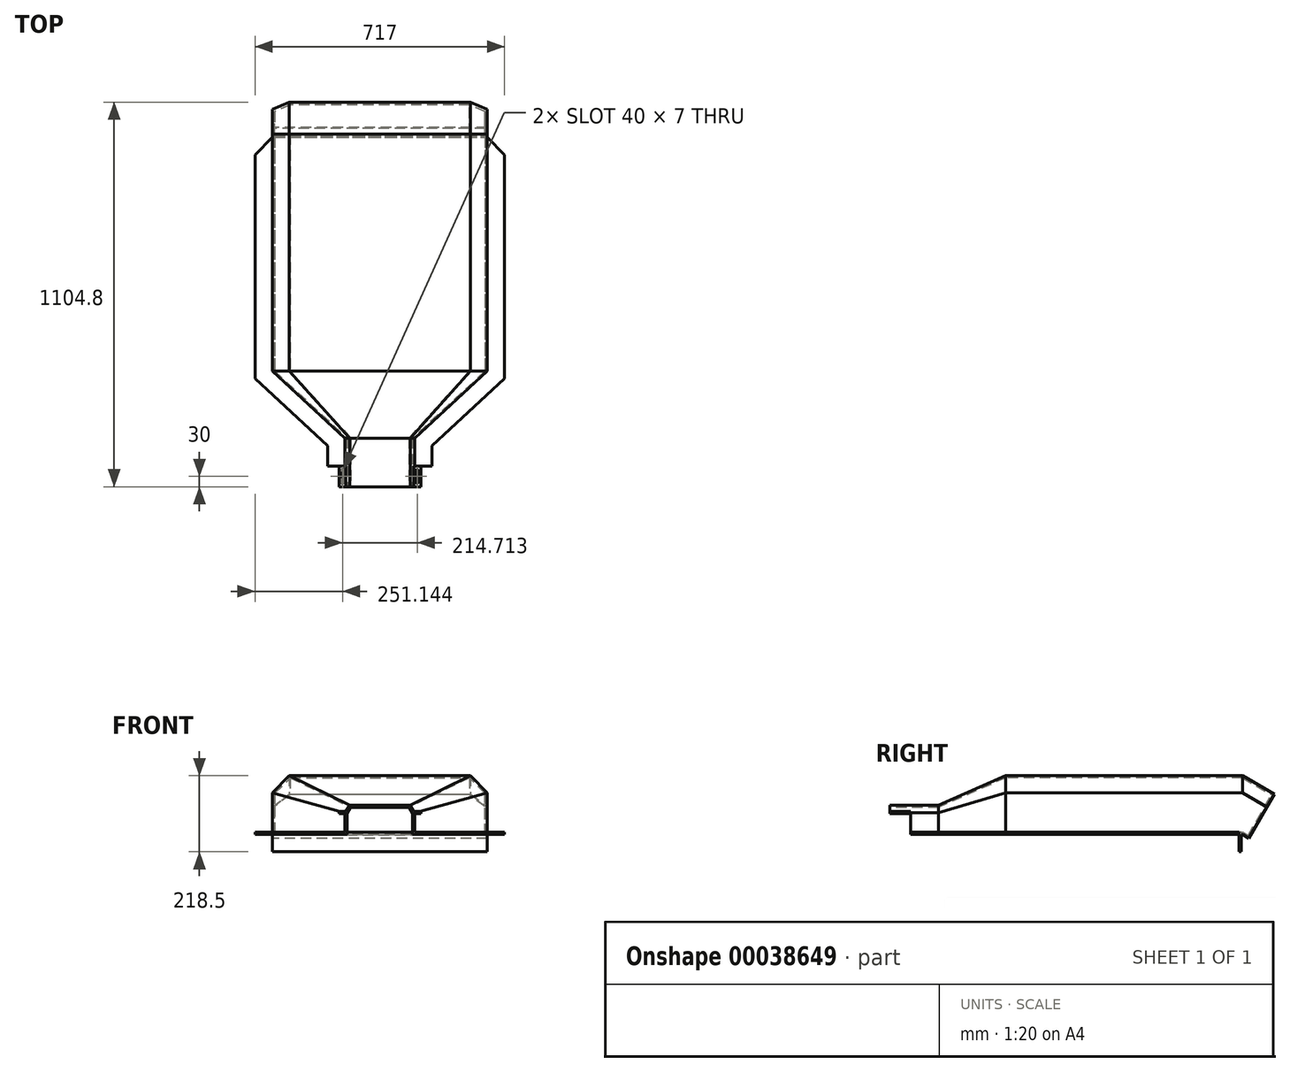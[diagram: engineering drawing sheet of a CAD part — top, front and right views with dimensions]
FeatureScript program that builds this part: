
annotation { "Feature Type Name" : "Feature", "Feature Type Description" : "" }
export const myFeature = defineFeature(function(context is Context, id is Id, definition is map)
    precondition{}
    {
        {
            var Q0;
            Q0=qCreatedBy(makeId("Front.planeOp"),FACE);
            var sketch = newSketch(context, id + "F0", { "sketchPlane" : qUnion([Q0])});
            skLineSegment(sketch, "E0", {"start": v(0, 78) * mm, "end": v(83.5, 78) * mm});
            skLineSegment(sketch, "E1", {"start": v(83.5, 78) * mm, "end": v(93.9, 60) * mm});
            skLineSegment(sketch, "E2", {"start": v(93.9, 60) * mm, "end": v(117.36, 60) * mm});
            skLineSegment(sketch, "E3", {"start": v(93.9, 60) * mm, "end": v(93.9, 0) * mm, "construction": true});
            skLineSegment(sketch, "E4.0", {"start": v(97.36, 66) * mm, "end": v(117.36, 66) * mm});
            skLineSegment(sketch, "E4.1", {"start": v(86.96, 84) * mm, "end": v(97.36, 66) * mm});
            skLineSegment(sketch, "E4.2", {"start": v(0, 84) * mm, "end": v(86.96, 84) * mm});
            skLineSegment(sketch, "E5", {"start": v(117.36, 60) * mm, "end": v(117.36, 66) * mm});
            skLineSegment(sketch, "E6", {"start": v(0, 78) * mm, "end": v(0, 84) * mm});
            skSolve(sketch);
        }
        {
            var Q0;
            Q0=makeQuery(id+"F0.imprint","IMPRINT",FACE,{"disambiguationData":[TD([[makeQuery(id+"F0.imprint","IMPRINT",EDGE,{"derivedFrom":sQuery(id+"F0.wireOp",EDGE,"E0")}),1.0]])]});
            extrude(context, id + "F1", {"entities" : qUnion([Q0]), "oppositeDirection" : true, "depth" : 40 * mm, "hasSecondDirection" : true, "secondDirectionOppositeDirection" : false, "secondDirectionDepth" : 20 * mm});
        }
        {
            var Q0;
            Q0=makeQuery(id+"F1.opExtrude","SWEPT_FACE",FACE,{"disambiguationData":[OSD([sQuery(id+"F0.wireOp",EDGE,"E4.0")])]});
            var sketch = newSketch(context, id + "F2", { "sketchPlane" : qUnion([Q0])});
            skLineSegment(sketch, "E7", {"start": v(107.36, 40) * mm, "end": v(107.36, -20) * mm, "construction": true});
            skLineSegment(sketch, "E8", {"start": v(97.36, 10) * mm, "end": v(117.36, 10) * mm, "construction": true});
            skArc(sketch, "E9", {"start": v(110.86, 26.5) * mm, "mid": v(107.36, 30) * mm, "end": v(103.86, 26.5) * mm});
            skArc(sketch, "E10", {"start": v(103.86, -6.5) * mm, "mid": v(107.36, -10) * mm, "end": v(110.86, -6.5) * mm});
            skLineSegment(sketch, "E11", {"start": v(110.86, 26.5) * mm, "end": v(110.86, -6.5) * mm});
            skLineSegment(sketch, "E12", {"start": v(103.86, 26.5) * mm, "end": v(103.86, -6.5) * mm});
            skLineSegment(sketch, "E13", {"start": v(107.36, 26.5) * mm, "end": v(107.36, -6.5) * mm, "construction": true});
            skPoint(sketch, "E14", {"position": v(107.36, 10) * mm});
            skSolve(sketch);
        }
        {
            var Q0;
            Q0 = qSketchRegion(id + "F2", true);
            extrude(context, id + "F3", {"entities" : qUnion([Q0]), "operationType" : NewBodyOperationType.REMOVE, "endBound" : BoundingType.THROUGH_ALL, "oppositeDirection" : true, "depth" : 25 * mm});
        }
        {
            var Q0;
            Q0=makeQuery(id+"F1.opExtrude","SWEPT_BODY",BODY,{"disambiguationData":[OSD([sQuery(id+"F0.wireOp",EDGE,"E0"),sQuery(id+"F0.wireOp",EDGE,"E1"),sQuery(id+"F0.wireOp",EDGE,"E2"),sQuery(id+"F0.wireOp",EDGE,"E4.0"),sQuery(id+"F0.wireOp",EDGE,"E4.1"),sQuery(id+"F0.wireOp",EDGE,"E4.2"),sQuery(id+"F0.wireOp",EDGE,"E5"),sQuery(id+"F0.wireOp",EDGE,"E6")])]});
            var Q1;
            Q1=qCreatedBy(makeId("Right.planeOp"),FACE);
            mirror(context, id + "F4", {"operationType" : NewBodyOperationType.ADD, "entities" : qUnion([Q0]), "mirrorPlane" : qUnion([Q1])});
        }
        {
            var Q0;
            {var subQ0=makeQuery(id+"F1.opExtrude","CAP_FACE",FACE,{"disambiguationData":[OSD([sQuery(id+"F0.wireOp",EDGE,"E0"),sQuery(id+"F0.wireOp",EDGE,"E1"),sQuery(id+"F0.wireOp",EDGE,"E2"),sQuery(id+"F0.wireOp",EDGE,"E4.0"),sQuery(id+"F0.wireOp",EDGE,"E4.1"),sQuery(id+"F0.wireOp",EDGE,"E4.2"),sQuery(id+"F0.wireOp",EDGE,"E5"),sQuery(id+"F0.wireOp",EDGE,"E6")])],"isStart":false});Q0=makeQuery(id+"F4.boolean.opBoolean","MERGE",FACE,{"derivedFrom":[subQ0,makeQuery(id+"F4.opPattern","COPY",FACE,{"derivedFrom":subQ0,"instanceName":"1"})]});}
            var sketch = newSketch(context, id + "F5", { "sketchPlane" : qUnion([Q0])});
            skLineSegment(sketch, "E15", {"start": v(0, 84) * mm, "end": v(0, 78) * mm});
            skLineSegment(sketch, "E16", {"start": v(0, 78) * mm, "end": v(83.5, 78) * mm});
            skLineSegment(sketch, "E17", {"start": v(83.5, 78) * mm, "end": v(93.9, 60) * mm});
            skLineSegment(sketch, "E18", {"start": v(93.9, 60) * mm, "end": v(93.9, 0) * mm});
            skLineSegment(sketch, "E19.0", {"start": v(86.96, 84) * mm, "end": v(0, 84) * mm});
            skLineSegment(sketch, "E20.0", {"start": v(86.96, 84) * mm, "end": v(99.9, 61.6) * mm});
            skLineSegment(sketch, "E21", {"start": v(93.9, 0) * mm, "end": v(99.9, 0) * mm});
            skLineSegment(sketch, "E22", {"start": v(99.9, 0) * mm, "end": v(99.9, 61.6) * mm});
            skPoint(sketch, "E23.orphan", {"position": v(-86.96, 84) * mm});
            skLineSegment(sketch, "E24.MirrorCS", {"start": v(-86.96, 84) * mm, "end": v(0, 84) * mm});
            skLineSegment(sketch, "E25.MirrorCS", {"start": v(0, 78) * mm, "end": v(-83.5, 78) * mm});
            skLineSegment(sketch, "E26.MirrorCS", {"start": v(-86.96, 84) * mm, "end": v(-99.9, 61.6) * mm});
            skLineSegment(sketch, "E27.MirrorCS", {"start": v(-83.5, 78) * mm, "end": v(-93.9, 60) * mm});
            skLineSegment(sketch, "E28.MirrorCS", {"start": v(-99.9, 0) * mm, "end": v(-99.9, 61.6) * mm});
            skLineSegment(sketch, "E29.MirrorCS", {"start": v(-93.9, 60) * mm, "end": v(-93.9, 0) * mm});
            skLineSegment(sketch, "E30.MirrorCS", {"start": v(-93.9, 0) * mm, "end": v(-99.9, 0) * mm});
            skSolve(sketch);
        }
        {
            var Q0;
            Q0=makeQuery(id+"F5.imprint","IMPRINT",FACE,{"disambiguationData":[TD([[makeQuery(id+"F5.imprint","IMPRINT",EDGE,{"derivedFrom":sQuery(id+"F5.wireOp",EDGE,"E15")}),1.0]])]});
            var Q1;
            Q1=makeQuery(id+"F5.imprint","IMPRINT",FACE,{"disambiguationData":[TD([[makeQuery(id+"F5.imprint","IMPRINT",EDGE,{"derivedFrom":sQuery(id+"F5.wireOp",EDGE,"E15")}),-1.0]])]});
            var Q2;
            {var subQ3=sQuery(id+"F5.wireOp",EDGE,"E29.MirrorCS");Q2=makeQuery(id+"F5.imprint","IMPRINT",FACE,{"disambiguationData":[TD([[makeQuery(id+"F5.imprint","IMPRINT",EDGE,{"derivedFrom":subQ3}),-1.0]])]});}
            var Q3;
            {var subQ3=sQuery(id+"F5.wireOp",EDGE,"E18");Q3=makeQuery(id+"F5.imprint","IMPRINT",FACE,{"disambiguationData":[TD([[makeQuery(id+"F5.imprint","IMPRINT",EDGE,{"derivedFrom":subQ3}),1.0]])]});}
            extrude(context, id + "F6", {"entities" : qUnion([Q0, Q1, Q2, Q3]), "operationType" : NewBodyOperationType.ADD, "depth" : 80 * mm});
        }
        {
            var Q0;
            Q0=qCreatedBy(makeId("Front.planeOp"),FACE);
            cPlane(context, id + "F7", {"entities" : qUnion([Q0]), "cplaneType" : CPlaneType.OFFSET, "offset" : 312.5 * mm, "oppositeDirection" : true, "width" : 150 * mm, "height" : 150 * mm});
        }
        {
            var Q0;
            Q0=qCreatedBy(id+"F7.planeOp",FACE);
            var sketch = newSketch(context, id + "F8", { "sketchPlane" : qUnion([Q0])});
            skLineSegment(sketch, "E31", {"start": v(0, 0) * mm, "end": v(302.5, 0) * mm, "construction": true});
            skLineSegment(sketch, "E32", {"start": v(302.5, 0) * mm, "end": v(302.5, 117.5) * mm});
            skLineSegment(sketch, "E33", {"start": v(302.5, 117.5) * mm, "end": v(257.5, 162.5) * mm});
            skLineSegment(sketch, "E34", {"start": v(257.5, 162.5) * mm, "end": v(0, 162.5) * mm});
            skLineSegment(sketch, "E35", {"start": v(0, 0) * mm, "end": v(0, 162.5) * mm, "construction": true});
            skPoint(sketch, "E36", {"position": v(280, 140) * mm});
            skLineSegment(sketch, "E37.0", {"start": v(259.99, 168.5) * mm, "end": v(0, 168.5) * mm});
            skLineSegment(sketch, "E37.1", {"start": v(308.5, 119.99) * mm, "end": v(259.99, 168.5) * mm});
            skLineSegment(sketch, "E37.2", {"start": v(308.5, 0) * mm, "end": v(308.5, 119.99) * mm});
            skLineSegment(sketch, "E38", {"start": v(302.5, 0) * mm, "end": v(308.5, 0) * mm});
            skLineSegment(sketch, "E39", {"start": v(0, 168.5) * mm, "end": v(0, 162.5) * mm, "construction": true});
            skLineSegment(sketch, "E40.MirrorCS", {"start": v(-259.99, 168.5) * mm, "end": v(0, 168.5) * mm});
            skLineSegment(sketch, "E41.MirrorCS", {"start": v(-257.5, 162.5) * mm, "end": v(0, 162.5) * mm});
            skLineSegment(sketch, "E42.MirrorCS", {"start": v(-308.5, 119.99) * mm, "end": v(-259.99, 168.5) * mm});
            skLineSegment(sketch, "E43.MirrorCS", {"start": v(-302.5, 117.5) * mm, "end": v(-257.5, 162.5) * mm});
            skLineSegment(sketch, "E44.MirrorCS", {"start": v(-302.5, 0) * mm, "end": v(-302.5, 117.5) * mm});
            skLineSegment(sketch, "E45.MirrorCS", {"start": v(-308.5, 0) * mm, "end": v(-308.5, 119.99) * mm});
            skLineSegment(sketch, "E46.MirrorCS", {"start": v(-302.5, 0) * mm, "end": v(-308.5, 0) * mm});
            skSolve(sketch);
        }
        {
            var Q0;
            Q0=makeQuery(id+"F8.imprint","IMPRINT",FACE,{"disambiguationData":[TD([[makeQuery(id+"F8.imprint","IMPRINT",EDGE,{"derivedFrom":sQuery(id+"F8.wireOp",EDGE,"E32")}),-1.0]])]});
            extrude(context, id + "F9", {"entities" : qUnion([Q0]), "oppositeDirection" : true, "depth" : 680.5 * mm});
        }
        {
            var Q0;
            Q0=makeQuery(id+"F9.opExtrude","CAP_FACE",FACE,{"disambiguationData":[OSD([sQuery(id+"F8.wireOp",EDGE,"E32"),sQuery(id+"F8.wireOp",EDGE,"E33"),sQuery(id+"F8.wireOp",EDGE,"E34"),sQuery(id+"F8.wireOp",EDGE,"E37.0"),sQuery(id+"F8.wireOp",EDGE,"E37.1"),sQuery(id+"F8.wireOp",EDGE,"E37.2"),sQuery(id+"F8.wireOp",EDGE,"E38"),sQuery(id+"F8.wireOp",EDGE,"E40.MirrorCS"),sQuery(id+"F8.wireOp",EDGE,"E41.MirrorCS"),sQuery(id+"F8.wireOp",EDGE,"E42.MirrorCS"),sQuery(id+"F8.wireOp",EDGE,"E43.MirrorCS"),sQuery(id+"F8.wireOp",EDGE,"E44.MirrorCS"),sQuery(id+"F8.wireOp",EDGE,"E45.MirrorCS"),sQuery(id+"F8.wireOp",EDGE,"E46.MirrorCS")])],"isStart":true});
            var Q1;
            Q1=makeQuery(id+"F6.opExtrude","CAP_FACE",FACE,{"disambiguationData":[OSD([sQuery(id+"F5.wireOp",EDGE,"E16"),sQuery(id+"F5.wireOp",EDGE,"E17"),sQuery(id+"F5.wireOp",EDGE,"E18"),sQuery(id+"F5.wireOp",EDGE,"E19.0"),sQuery(id+"F5.wireOp",EDGE,"E20.0"),sQuery(id+"F5.wireOp",EDGE,"E21"),sQuery(id+"F5.wireOp",EDGE,"E22"),sQuery(id+"F5.wireOp",EDGE,"E24.MirrorCS"),sQuery(id+"F5.wireOp",EDGE,"E25.MirrorCS"),sQuery(id+"F5.wireOp",EDGE,"E26.MirrorCS"),sQuery(id+"F5.wireOp",EDGE,"E27.MirrorCS"),sQuery(id+"F5.wireOp",EDGE,"E28.MirrorCS"),sQuery(id+"F5.wireOp",EDGE,"E29.MirrorCS"),sQuery(id+"F5.wireOp",EDGE,"E30.MirrorCS")])],"isStart":false});
            loft(context, id + "F10", {"operationType" : NewBodyOperationType.ADD, "sheetProfilesArray" : [{ "sheetProfileEntities" : qUnion([Q0]) }, { "sheetProfileEntities" : qUnion([Q1]) }]});
        }
        {
            var Q0;
            Q0=makeQuery(id+"F9.opExtrude","CAP_EDGE",EDGE,{"disambiguationData":[OSD([sQuery(id+"F8.wireOp",EDGE,"E37.0"),sQuery(id+"F8.wireOp",EDGE,"E40.MirrorCS")])],"isStart":false});
            cPlane(context, id + "F11", {"entities" : qUnion([Q0]), "cplaneType" : CPlaneType.LINE_ANGLE, "offset" : 150 * mm, "angle" : 30 * degree, "width" : 150 * mm, "height" : 150 * mm});
        }
        {
            var Q0;
            Q0=qCreatedBy(id+"F11.planeOp",FACE);
            cPlane(context, id + "F12", {"entities" : qUnion([Q0]), "cplaneType" : CPlaneType.OFFSET, "offset" : 100 * mm, "oppositeDirection" : true, "width" : 150 * mm, "height" : 150 * mm});
        }
        {
            var Q0;
            Q0=qCreatedBy(id+"F12.planeOp",FACE);
            var sketch = newSketch(context, id + "F13", { "sketchPlane" : qUnion([Q0])});
            skLineSegment(sketch, "E47.0.0", {"start": v(302.5, 496.5) * mm, "end": v(302.5, 598.26) * mm});
            skLineSegment(sketch, "E47.0.1", {"start": v(302.5, 598.26) * mm, "end": v(257.5, 637.23) * mm});
            skLineSegment(sketch, "E47.0.2", {"start": v(257.5, 637.23) * mm, "end": v(-257.5, 637.23) * mm});
            skLineSegment(sketch, "E47.0.3", {"start": v(-257.5, 637.23) * mm, "end": v(-302.5, 598.26) * mm});
            skLineSegment(sketch, "E47.0.4", {"start": v(-302.5, 598.26) * mm, "end": v(-302.5, 496.5) * mm});
            skLineSegment(sketch, "E47.0.5", {"start": v(-302.5, 496.5) * mm, "end": v(-308.5, 496.5) * mm});
            skLineSegment(sketch, "E47.0.6", {"start": v(-308.5, 496.5) * mm, "end": v(-308.5, 600.41) * mm});
            skLineSegment(sketch, "E47.0.7", {"start": v(-308.5, 600.41) * mm, "end": v(-259.99, 642.43) * mm});
            skLineSegment(sketch, "E47.0.8", {"start": v(-259.99, 642.43) * mm, "end": v(259.99, 642.43) * mm});
            skLineSegment(sketch, "E47.0.9", {"start": v(259.99, 642.43) * mm, "end": v(308.5, 600.41) * mm});
            skLineSegment(sketch, "E47.0.10", {"start": v(308.5, 600.41) * mm, "end": v(308.5, 496.5) * mm});
            skLineSegment(sketch, "E47.0.11", {"start": v(308.5, 496.5) * mm, "end": v(302.5, 496.5) * mm});
            skSolve(sketch);
        }
        {
            var Q0;
            Q0=makeQuery(id+"F13.imprint","IMPRINT",FACE,{"disambiguationData":[TD([[makeQuery(id+"F13.imprint","IMPRINT",EDGE,{"derivedFrom":sQuery(id+"F13.wireOp",EDGE,"E47.0.0")}),-1.0]])]});
            var Q1;
            Q1=makeQuery(id+"F1.opExtrude","SWEPT_BODY",BODY,{"disambiguationData":[OSD([sQuery(id+"F0.wireOp",EDGE,"E0"),sQuery(id+"F0.wireOp",EDGE,"E1"),sQuery(id+"F0.wireOp",EDGE,"E2"),sQuery(id+"F0.wireOp",EDGE,"E4.0"),sQuery(id+"F0.wireOp",EDGE,"E4.1"),sQuery(id+"F0.wireOp",EDGE,"E4.2"),sQuery(id+"F0.wireOp",EDGE,"E5"),sQuery(id+"F0.wireOp",EDGE,"E6")])]});
            extrude(context, id + "F14", {"entities" : qUnion([Q0]), "operationType" : NewBodyOperationType.ADD, "endBound" : BoundingType.UP_TO_BODY, "endBoundEntityBody" : qUnion([Q1]), "depth" : 25 * mm});
        }
        {
            var Q0;
            Q0=makeQuery(id+"F14.opExtrude","CAP_FACE",FACE,{"disambiguationData":[OSD([sQuery(id+"F13.wireOp",EDGE,"E47.0.0"),sQuery(id+"F13.wireOp",EDGE,"E47.0.1"),sQuery(id+"F13.wireOp",EDGE,"E47.0.2"),sQuery(id+"F13.wireOp",EDGE,"E47.0.3"),sQuery(id+"F13.wireOp",EDGE,"E47.0.4"),sQuery(id+"F13.wireOp",EDGE,"E47.0.5"),sQuery(id+"F13.wireOp",EDGE,"E47.0.6"),sQuery(id+"F13.wireOp",EDGE,"E47.0.7"),sQuery(id+"F13.wireOp",EDGE,"E47.0.8"),sQuery(id+"F13.wireOp",EDGE,"E47.0.9"),sQuery(id+"F13.wireOp",EDGE,"E47.0.10"),sQuery(id+"F13.wireOp",EDGE,"E47.0.11")])],"isStart":true});
            var sketch = newSketch(context, id + "F15", { "sketchPlane" : qUnion([Q0])});
            skLineSegment(sketch, "E48.0", {"start": v(259.99, 642.43) * mm, "end": v(-259.99, 642.43) * mm});
            skLineSegment(sketch, "E48.1", {"start": v(308.5, 600.41) * mm, "end": v(259.99, 642.43) * mm});
            skLineSegment(sketch, "E48.2", {"start": v(308.5, 496.5) * mm, "end": v(308.5, 600.41) * mm});
            skLineSegment(sketch, "E48.3", {"start": v(-259.99, 642.43) * mm, "end": v(-308.5, 600.41) * mm});
            skLineSegment(sketch, "E48.4", {"start": v(-308.5, 600.41) * mm, "end": v(-308.5, 496.5) * mm});
            skLineSegment(sketch, "E49", {"start": v(-308.5, 496.5) * mm, "end": v(308.5, 496.5) * mm});
            skSolve(sketch);
        }
        {
            var Q0;
            Q0 = qSketchRegion(id + "F15", true);
            extrude(context, id + "F16", {"entities" : qUnion([Q0]), "operationType" : NewBodyOperationType.ADD, "depth" : 6 * mm});
        }
        {
            var Q0;
            Q0=makeQuery(id+"F16.boolean.opBoolean","MERGE",FACE,{"derivedFrom":[makeQuery(id+"F14.opExtrude","SWEPT_FACE",FACE,{"disambiguationData":[OSD([sQuery(id+"F13.wireOp",EDGE,"E47.0.5")])]}),makeQuery(id+"F14.opExtrude","SWEPT_FACE",FACE,{"disambiguationData":[OSD([sQuery(id+"F13.wireOp",EDGE,"E47.0.11")])]}),makeQuery(id+"F16.opExtrude","SWEPT_FACE",FACE,{"disambiguationData":[OSD([sQuery(id+"F15.wireOp",EDGE,"E49")])]})]});
            var sketch = newSketch(context, id + "F17", { "sketchPlane" : qUnion([Q0])});
            skLineSegment(sketch, "E50.0", {"start": v(302.5, -859.96) * mm, "end": v(308.5, -859.96) * mm, "construction": true});
            skLineSegment(sketch, "E50.1", {"start": v(308.5, -881.71) * mm, "end": v(-308.5, -881.71) * mm});
            skLineSegment(sketch, "E51.0", {"start": v(-302.5, -859.96) * mm, "end": v(-308.5, -859.96) * mm, "construction": true});
            skLineSegment(sketch, "E52.bottom", {"start": v(308.5, -859.96) * mm, "end": v(-308.5, -859.96) * mm});
            skLineSegment(sketch, "E52.top", {"start": v(308.5, -881.71) * mm, "end": v(-308.5, -881.71) * mm, "construction": true});
            skLineSegment(sketch, "E52.left", {"start": v(308.5, -859.96) * mm, "end": v(308.5, -881.71) * mm, "construction": true});
            skLineSegment(sketch, "E52.right", {"start": v(-308.5, -859.96) * mm, "end": v(-308.5, -881.71) * mm, "construction": true});
            skLineSegment(sketch, "E53", {"start": v(-308.5, -881.71) * mm, "end": v(-308.5, -859.96) * mm});
            skLineSegment(sketch, "E54", {"start": v(308.5, -859.96) * mm, "end": v(308.5, -881.71) * mm});
            skSolve(sketch);
        }
        {
            var Q0;
            Q0=makeQuery(id+"F17.imprint","IMPRINT",FACE,{"disambiguationData":[TD([[makeQuery(id+"F17.imprint","IMPRINT",EDGE,{"derivedFrom":sQuery(id+"F17.wireOp",EDGE,"E50.1")}),-1.0]])]});
            var Q1;
            Q1=makeQuery(id+"F17.imprint","IMPRINT",FACE,{"disambiguationData":[TD([[makeQuery(id+"F17.imprint","IMPRINT",EDGE,{"derivedFrom":makeQuery(id+"F16.opExtrude","CAP_EDGE",EDGE,{"disambiguationData":[OSD([sQuery(id+"F15.wireOp",EDGE,"E49")])],"isStart":true})}),-1.0]])]});
            extrude(context, id + "F18", {"entities" : qUnion([Q0, Q1]), "operationType" : NewBodyOperationType.ADD, "oppositeDirection" : true, "depth" : 6 * mm});
        }
        {
            var Q0;
            Q0=qCreatedBy(makeId("Front.planeOp"),FACE);
            cPlane(context, id + "F19", {"entities" : qUnion([Q0]), "cplaneType" : CPlaneType.OFFSET, "offset" : 990 * mm, "oppositeDirection" : true, "width" : 150 * mm, "height" : 150 * mm});
        }
        {
            var Q0;
            Q0=qCreatedBy(id+"F19.planeOp",FACE);
            var sketch = newSketch(context, id + "F20", { "sketchPlane" : qUnion([Q0])});
            skLineSegment(sketch, "E55.0", {"start": v(-302.5, 0) * mm, "end": v(302.5, 0) * mm});
            skLineSegment(sketch, "E56", {"start": v(302.5, 0) * mm, "end": v(302.5, 6) * mm});
            skLineSegment(sketch, "E57", {"start": v(-302.5, 0) * mm, "end": v(-302.5, 6) * mm});
            skLineSegment(sketch, "E58", {"start": v(-302.5, 6) * mm, "end": v(302.5, 6) * mm});
            skSolve(sketch);
        }
        {
            var Q1;
            Q1=makeQuery(id+"F18.opExtrude","SWEPT_FACE",FACE,{"disambiguationData":[OSD([sQuery(id+"F17.wireOp",EDGE,"E52.bottom")])]});
            var Q2;
            Q2=makeQuery(id+"F20.imprint","IMPRINT",FACE,{"disambiguationData":[TD([[makeQuery(id+"F20.imprint","IMPRINT",EDGE,{"derivedFrom":sQuery(id+"F20.wireOp",EDGE,"E55.0")}),1.0]])]});
            loft(context, id + "F21", {"operationType" : NewBodyOperationType.ADD, "sheetProfilesArray" : [{ "sheetProfileEntities" : qUnion([Q1]) }, { "sheetProfileEntities" : qUnion([Q2]) }]});
        }
        {
            var Q0;
            Q0=qCreatedBy(id+"F19.planeOp",FACE);
            var sketch = newSketch(context, id + "F22", { "sketchPlane" : qUnion([Q0])});
            skPoint(sketch, "E59.0", {"position": v(-308.5, 0) * mm});
            skPoint(sketch, "E60.1", {"position": v(308.5, 0) * mm});
            skPoint(sketch, "E61.0", {"position": v(-302.5, 6) * mm});
            skLineSegment(sketch, "E62", {"start": v(-308.5, 6) * mm, "end": v(308.5, 6) * mm});
            skLineSegment(sketch, "E63", {"start": v(308.5, -50) * mm, "end": v(308.5, 6) * mm});
            skLineSegment(sketch, "E64", {"start": v(-308.5, -50) * mm, "end": v(-308.5, 6) * mm});
            skLineSegment(sketch, "E65", {"start": v(-308.5, -50) * mm, "end": v(308.5, -50) * mm});
            skSolve(sketch);
        }
        {
            var Q0;
            Q0 = qSketchRegion(id + "F22", true);
            extrude(context, id + "F23", {"entities" : qUnion([Q0]), "operationType" : NewBodyOperationType.ADD, "depth" : 6 * mm});
        }
        {
            var Q0;
            {var subQ0=sQuery(id+"F5.wireOp",EDGE,"E21");var subQ1=sQuery(id+"F8.wireOp",EDGE,"E46.MirrorCS");var subQ2=sQuery(id+"F5.wireOp",EDGE,"E18");var subQ3=sQuery(id+"F5.wireOp",EDGE,"E22");var subQ4=sQuery(id+"F8.wireOp",EDGE,"E44.MirrorCS");var subQ5=sQuery(id+"F8.wireOp",EDGE,"E45.MirrorCS");var subQ6=sQuery(id+"F5.wireOp",EDGE,"E30.MirrorCS");var subQ7=sQuery(id+"F8.wireOp",EDGE,"E38");var subQ8=sQuery(id+"F5.wireOp",EDGE,"E28.MirrorCS");var subQ9=sQuery(id+"F5.wireOp",EDGE,"E29.MirrorCS");var subQ10=sQuery(id+"F8.wireOp",EDGE,"E32");var subQ11=sQuery(id+"F8.wireOp",EDGE,"E37.2");var subQ12=sQuery(id+"F8.wireOp",EDGE,"E33");var subQ13=sQuery(id+"F8.wireOp",EDGE,"E37.1");var subQ14=sQuery(id+"F13.wireOp",EDGE,"E47.0.0");Q0=makeQuery(id+"F23.boolean.opBoolean","SPLIT",FACE,{"disambiguationData":[TD([makeQuery(id+"F6.opExtrude","SWEPT_FACE",FACE,{"disambiguationData":[OSD([subQ8])]})])],"derivedFrom":makeQuery(id+"F21.boolean.opBoolean","MERGE",FACE,{"derivedFrom":[makeQuery(id+"F10.boolean.opBoolean","MERGE",FACE,{"derivedFrom":[makeQuery(id+"F6.opExtrude","SWEPT_FACE",FACE,{"disambiguationData":[OSD([subQ0])]}),makeQuery(id+"F9.opExtrude","SWEPT_FACE",FACE,{"disambiguationData":[OSD([subQ1])]}),makeQuery(id+"F10.opLoft","SWEPT_FACE",FACE,{"disambiguationData":[OSD([subQ2,subQ0,subQ3,subQ4,subQ5,subQ1])]})]}),makeQuery(id+"F10.boolean.opBoolean","MERGE",FACE,{"derivedFrom":[makeQuery(id+"F6.opExtrude","SWEPT_FACE",FACE,{"disambiguationData":[OSD([subQ6])]}),makeQuery(id+"F9.opExtrude","SWEPT_FACE",FACE,{"disambiguationData":[OSD([subQ7])]}),makeQuery(id+"F10.opLoft","SWEPT_FACE",FACE,{"disambiguationData":[OSD([subQ8,subQ9,subQ6,subQ10,subQ11,subQ7])]})]}),makeQuery(id+"F21.opLoft","SWEPT_FACE",FACE,{"disambiguationData":[OSD([subQ10,subQ12,sQuery(id+"F8.wireOp",EDGE,"E34"),sQuery(id+"F8.wireOp",EDGE,"E37.0"),subQ13,subQ11,subQ7,sQuery(id+"F8.wireOp",EDGE,"E40.MirrorCS"),sQuery(id+"F8.wireOp",EDGE,"E41.MirrorCS"),sQuery(id+"F8.wireOp",EDGE,"E42.MirrorCS"),sQuery(id+"F8.wireOp",EDGE,"E43.MirrorCS"),subQ4,subQ5,subQ1,subQ14,sQuery(id+"F13.wireOp",EDGE,"E47.0.11"),sQuery(id+"F17.wireOp",EDGE,"E52.bottom"),sQuery(id+"F20.wireOp",EDGE,"E55.0"),sQuery(id+"F20.wireOp",EDGE,"E56"),sQuery(id+"F20.wireOp",EDGE,"E57")])]})]})});}
            var sketch = newSketch(context, id + "F24", { "sketchPlane" : qUnion([Q0])});
            skLineSegment(sketch, "E66.0", {"start": v(149.9, -98.1) * mm, "end": v(149.9, -40) * mm});
            skLineSegment(sketch, "E66.1", {"start": v(358.5, -290.6) * mm, "end": v(149.9, -98.1) * mm});
            skLineSegment(sketch, "E66.2", {"start": v(358.5, -934) * mm, "end": v(358.5, -290.6) * mm});
            skLineSegment(sketch, "E67", {"start": v(308.5, -984) * mm, "end": v(358.5, -934) * mm});
            skLineSegment(sketch, "E68", {"start": v(149.9, -40) * mm, "end": v(99.9, -40) * mm});
            skLineSegment(sketch, "E69.0", {"start": v(99.9, -120) * mm, "end": v(99.9, -40) * mm});
            skLineSegment(sketch, "E70.0", {"start": v(308.5, -312.5) * mm, "end": v(99.9, -120) * mm});
            skLineSegment(sketch, "E71.0", {"start": v(308.5, -984) * mm, "end": v(308.5, -312.5) * mm});
            skSolve(sketch);
        }
        {
            var Q0;
            Q0=makeQuery(id+"F24.imprint","IMPRINT",FACE,{"disambiguationData":[TD([[makeQuery(id+"F24.imprint","IMPRINT",EDGE,{"derivedFrom":sQuery(id+"F24.wireOp",EDGE,"E66.0")}),1.0]])]});
            extrude(context, id + "F25", {"entities" : qUnion([Q0]), "operationType" : NewBodyOperationType.ADD, "oppositeDirection" : true, "depth" : 6 * mm});
        }
        {
            var Q0;
            {var subQ0=sQuery(id+"F5.wireOp",EDGE,"E21");var subQ1=sQuery(id+"F8.wireOp",EDGE,"E46.MirrorCS");var subQ2=sQuery(id+"F5.wireOp",EDGE,"E18");var subQ3=sQuery(id+"F5.wireOp",EDGE,"E22");var subQ4=sQuery(id+"F8.wireOp",EDGE,"E44.MirrorCS");var subQ5=sQuery(id+"F8.wireOp",EDGE,"E45.MirrorCS");var subQ6=sQuery(id+"F5.wireOp",EDGE,"E30.MirrorCS");var subQ7=sQuery(id+"F8.wireOp",EDGE,"E38");var subQ8=sQuery(id+"F5.wireOp",EDGE,"E28.MirrorCS");var subQ9=sQuery(id+"F5.wireOp",EDGE,"E29.MirrorCS");var subQ10=sQuery(id+"F8.wireOp",EDGE,"E32");var subQ11=sQuery(id+"F8.wireOp",EDGE,"E37.2");var subQ12=sQuery(id+"F8.wireOp",EDGE,"E42.MirrorCS");var subQ13=sQuery(id+"F8.wireOp",EDGE,"E43.MirrorCS");Q0=makeQuery(id+"F23.boolean.opBoolean","SPLIT",FACE,{"disambiguationData":[TD([makeQuery(id+"F6.opExtrude","SWEPT_FACE",FACE,{"disambiguationData":[OSD([subQ2])]})])],"derivedFrom":makeQuery(id+"F21.boolean.opBoolean","MERGE",FACE,{"derivedFrom":[makeQuery(id+"F10.boolean.opBoolean","MERGE",FACE,{"derivedFrom":[makeQuery(id+"F6.opExtrude","SWEPT_FACE",FACE,{"disambiguationData":[OSD([subQ0])]}),makeQuery(id+"F9.opExtrude","SWEPT_FACE",FACE,{"disambiguationData":[OSD([subQ1])]}),makeQuery(id+"F10.opLoft","SWEPT_FACE",FACE,{"disambiguationData":[OSD([subQ2,subQ0,subQ3,subQ4,subQ5,subQ1])]})]}),makeQuery(id+"F10.boolean.opBoolean","MERGE",FACE,{"derivedFrom":[makeQuery(id+"F6.opExtrude","SWEPT_FACE",FACE,{"disambiguationData":[OSD([subQ6])]}),makeQuery(id+"F9.opExtrude","SWEPT_FACE",FACE,{"disambiguationData":[OSD([subQ7])]}),makeQuery(id+"F10.opLoft","SWEPT_FACE",FACE,{"disambiguationData":[OSD([subQ8,subQ9,subQ6,subQ10,subQ11,subQ7])]})]}),makeQuery(id+"F21.opLoft","SWEPT_FACE",FACE,{"disambiguationData":[OSD([subQ10,sQuery(id+"F8.wireOp",EDGE,"E33"),sQuery(id+"F8.wireOp",EDGE,"E34"),sQuery(id+"F8.wireOp",EDGE,"E37.0"),sQuery(id+"F8.wireOp",EDGE,"E37.1"),subQ11,subQ7,sQuery(id+"F8.wireOp",EDGE,"E40.MirrorCS"),sQuery(id+"F8.wireOp",EDGE,"E41.MirrorCS"),subQ12,subQ13,subQ4,subQ5,subQ1,sQuery(id+"F13.wireOp",EDGE,"E47.0.0"),sQuery(id+"F13.wireOp",EDGE,"E47.0.11"),sQuery(id+"F17.wireOp",EDGE,"E52.bottom"),sQuery(id+"F20.wireOp",EDGE,"E55.0"),sQuery(id+"F20.wireOp",EDGE,"E56"),sQuery(id+"F20.wireOp",EDGE,"E57")])]})]})});}
            var sketch = newSketch(context, id + "F26", { "sketchPlane" : qUnion([Q0])});
            skLineSegment(sketch, "E72.0", {"start": v(-149.9, -98.1) * mm, "end": v(-149.9, -40) * mm});
            skLineSegment(sketch, "E72.1", {"start": v(-358.5, -290.6) * mm, "end": v(-149.9, -98.1) * mm});
            skLineSegment(sketch, "E72.2", {"start": v(-358.5, -934) * mm, "end": v(-358.5, -290.6) * mm});
            skLineSegment(sketch, "E73", {"start": v(-93.9, -40) * mm, "end": v(-149.9, -40) * mm});
            skLineSegment(sketch, "E74", {"start": v(-308.5, -984) * mm, "end": v(-358.5, -934) * mm});
            skSolve(sketch);
        }
        {
            var Q0;
            {var subQ12=sQuery(id+"F26.wireOp",EDGE,"E72.0");Q0=makeQuery(id+"F26.imprint","IMPRINT",FACE,{"disambiguationData":[TD([[makeQuery(id+"F26.imprint","IMPRINT",EDGE,{"derivedFrom":subQ12}),-1.0]])]});}
            extrude(context, id + "F27", {"entities" : qUnion([Q0]), "operationType" : NewBodyOperationType.ADD, "oppositeDirection" : true, "depth" : 6 * mm});
        }
    });
